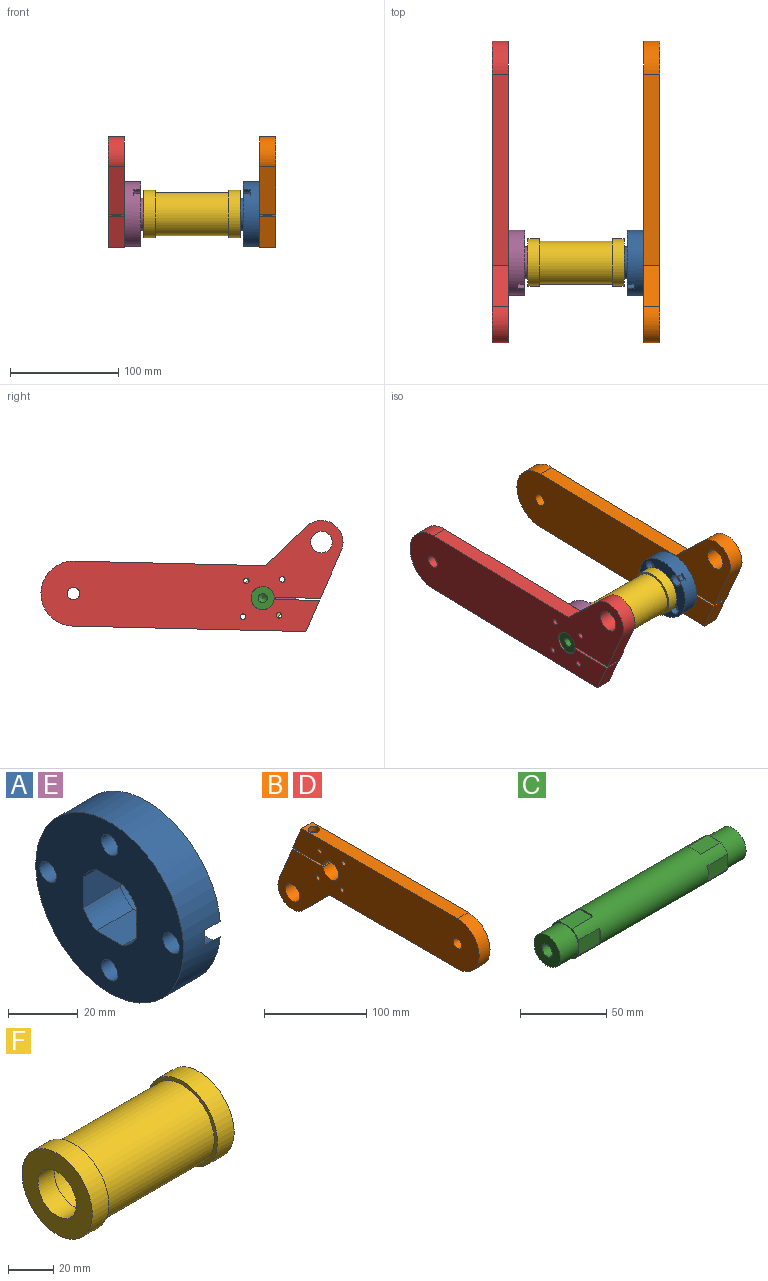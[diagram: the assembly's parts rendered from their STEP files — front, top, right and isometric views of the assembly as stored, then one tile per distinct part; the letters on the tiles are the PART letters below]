
ASSEMBLY  parts=6 mates=4
PART A: 27 faces, bbox 18x60x60 mm
  f0: cylinder r=12mm len=15mm, axis (-1,0,0), area 117mm2, adj f6,f7,f24,f26
  f1: cylinder r=12mm len=15mm, axis (-1,0,0), area 117mm2, adj f6,f7,f23,f25
  f2: cylinder r=12mm len=15mm, axis (-1,0,0), area 117mm2, adj f6,f7,f24,f25
  f3: cylinder r=12mm len=15mm, axis (-1,0,0), area 117mm2, adj f6,f7,f23,f26
  f4: cylinder r=30mm len=60mm, axis (-1,0,0), area 2760mm2, adj f5,f7,f14,f15,f20,f21
  f5: plane 60x59.77mm, normal (1,0,0), area 1758.7mm2, adj f4,f9,f13,f15,f19,f21
  f6: plane 25.75x25.75mm, normal (1,0,0), area 104.3mm2, adj f0,f1,f2,f3,f8,f23,f24,f25
  f7: plane 60x60mm, normal (-1,0,0), area 2267.6mm2, adj f0,f1,f2,f3,f4,f11,f16,f17
  f8: cylinder r=12.88mm len=25.75mm, axis (-1,0,0), area 242.7mm2, adj f6,f10
  f9: cylinder r=14.76mm len=29.53mm, axis (-1,0,0), area 278.3mm2, adj f5,f10
  f10: plane 29.53x29.53mm, normal (1,0,0), area 164mm2, adj f8,f9
  f11: cylinder r=3.38mm len=8.65mm, axis (1,0,0), area 183.6mm2, adj f7,f12
  f12: plane 11.11x11.11mm, normal (1,0,0), area 61.1mm2, adj f11,f13
  f13: cylinder r=5.56mm len=11.11mm, axis (1,0,0), area 221.7mm2, adj f5,f12
  f14: plane 11.11x10.56mm, normal (1,0,0), area 59.1mm2, adj f4,f15,f16
  f15: cylinder r=5.56mm len=11.11mm, axis (1,0,0), area 186.6mm2, adj f4,f5,f14
  f16: cylinder r=3.38mm len=8.65mm, axis (1,0,0), area 183.6mm2, adj f7,f14
  f17: cylinder r=3.38mm len=8.65mm, axis (1,0,0), area 183.6mm2, adj f7,f18
  f18: plane 11.11x11.11mm, normal (1,0,0), area 61.1mm2, adj f17,f19
  f19: cylinder r=5.56mm len=11.11mm, axis (1,0,0), area 221.7mm2, adj f5,f18
  f20: plane 11.11x10.56mm, normal (1,0,0), area 59.1mm2, adj f4,f21,f22
  f21: cylinder r=5.56mm len=11.11mm, axis (1,0,0), area 186.6mm2, adj f4,f5,f20
  f22: cylinder r=3.38mm len=8.65mm, axis (1,0,0), area 183.6mm2, adj f7,f20
  f23: plane 15x10.67mm, normal (0,0,-1), area 160mm2, adj f1,f3,f6,f7
  f24: plane 15x10.67mm, normal (0,0,1), area 160mm2, adj f0,f2,f6,f7
  f25: plane 15x10.67mm, normal (0,-1,0), area 160mm2, adj f1,f2,f6,f7
  f26: plane 15x10.67mm, normal (0,1,0), area 160mm2, adj f0,f3,f6,f7
PART B: 23 faces, bbox 15x278x103 mm
  f0: plane 278.03x103.03mm, normal (1,0,0), area 16118.8mm2, adj f1,f2,f3,f4,f6,f7,f8,f9
  f1: plane 29x15mm, normal (0,0.93,0.38), area 469.8mm2, adj f0,f3,f5,f15
  f2: plane 176.72x15mm, normal (0,0,-1), area 2650.7mm2, adj f0,f4,f5,f11
  f3: plane 215.75x15mm, normal (0,0,1), area 3139.3mm2, adj f0,f1,f4,f5,f19
  f4: cylinder r=30mm len=60mm, axis (-1,0,0), area 1413.7mm2, adj f0,f2,f3,f5
  f5: plane 278.03x103.03mm, normal (-1,0,0), area 16118.8mm2, adj f1,f2,f3,f4,f6,f7,f8,f9
  f6: cylinder r=5.75mm len=15mm, axis (1,0,0), area 542.3mm2, adj f0,f5
  f7: cylinder r=2.55mm len=15mm, axis (1,0,0), area 240.6mm2, adj f0,f5
  f8: cylinder r=2.55mm len=15mm, axis (1,0,0), area 240.6mm2, adj f0,f5
  f9: cylinder r=2.55mm len=15mm, axis (1,0,0), area 240.6mm2, adj f0,f5
  f10: cylinder r=2.55mm len=15mm, axis (1,0,0), area 240.6mm2, adj f0,f5
  f11: plane 37.18x37.18mm, normal (0,-0.71,-0.71), area 788.6mm2, adj f0,f2,f5,f12
  f12: cylinder r=20mm len=34.14mm, axis (1,0,0), area 823.1mm2, adj f0,f5,f11,f14
  f13: cylinder r=10mm len=20mm, axis (1,0,0), area 942.5mm2, adj f0,f5
  f14: plane 44.48x18.15mm, normal (0,0.93,0.38), area 720.6mm2, adj f0,f5,f12,f16
  f15: plane 41.88x15mm, normal (0,0,-1), area 592.4mm2, adj f0,f1,f5,f17,f22
  f16: plane 42.7x15mm, normal (0,0,1), area 617.5mm2, adj f0,f5,f14,f20,f22
  f17: cylinder r=3.38mm len=22.65mm, axis (0,0,1), area 480.8mm2, adj f15,f18
  f18: plane 11.11x11.11mm, normal (0,0,1), area 61.1mm2, adj f17,f19
  f19: cylinder r=5.56mm len=11.11mm, axis (0,0,1), area 221.7mm2, adj f3,f18
  f20: cylinder r=2.71mm len=29mm, axis (0,0,1), area 492.9mm2, adj f16,f21
  f21: cone r=0mm half-angle=59deg, axis (0,0,1), area 26.8mm2, adj f20
  f22: cylinder r=10.75mm len=21.5mm, axis (1,0,0), area 983.1mm2, adj f0,f5,f15,f16
PART C: 33 faces, bbox 152x24x24 mm
  f0: plane 17x10.67mm, normal (0,-1,0), area 181.3mm2, adj f12,f24,f26,f28
  f1: plane 17x10.67mm, normal (0,0,1), area 181.3mm2, adj f13,f24,f26,f27
  f2: plane 17x10.67mm, normal (0,1,0), area 181.3mm2, adj f14,f24,f27,f29
  f3: plane 17x10.67mm, normal (0,0,-1), area 181.3mm2, adj f15,f24,f28,f29
  f4: plane 21.5x21.5mm, normal (1,0,0), area 307.2mm2, adj f5,f7
  f5: cylinder r=4.22mm len=20mm, axis (1,0,0), area 529.8mm2, adj f4,f6
  f6: cone r=0mm half-angle=59deg, axis (1,0,0), area 65.2mm2, adj f5
  f7: cylinder r=10.75mm len=21.5mm, axis (1,0,0), area 1013.2mm2, adj f4,f8,f9,f10,f11
  f8: plane 10.75x10.75mm, normal (1,0,0), area 13.4mm2, adj f7,f20,f23,f24
  f9: plane 10.75x10.75mm, normal (1,0,0), area 13.4mm2, adj f7,f20,f21,f24
  f10: plane 10.75x10.75mm, normal (1,0,0), area 13.4mm2, adj f7,f21,f22,f24
  f11: plane 10.75x10.75mm, normal (1,0,0), area 13.4mm2, adj f7,f22,f23,f24
  f12: plane 10.67x1.25mm, normal (-1,0,0), area 9mm2, adj f0,f24
  f13: plane 10.67x1.25mm, normal (-1,0,0), area 9mm2, adj f1,f24
  f14: plane 10.67x1.25mm, normal (-1,0,0), area 9mm2, adj f2,f24
  f15: plane 10.67x1.25mm, normal (-1,0,0), area 9mm2, adj f3,f24
  f16: plane 10.67x1.25mm, normal (1,0,0), area 9mm2, adj f23,f24
  f17: plane 10.67x1.25mm, normal (1,0,0), area 9mm2, adj f21,f24
  f18: plane 10.67x1.25mm, normal (1,0,0), area 9mm2, adj f20,f24
  f19: plane 10.67x1.25mm, normal (1,0,0), area 9mm2, adj f22,f24
  f20: plane 17x10.67mm, normal (0,0,1), area 181.3mm2, adj f8,f9,f18,f24
  f21: plane 17x10.67mm, normal (0,-1,0), area 181.3mm2, adj f9,f10,f17,f24
  f22: plane 17x10.67mm, normal (0,0,-1), area 181.3mm2, adj f10,f11,f19,f24
  f23: plane 17x10.67mm, normal (0,1,0), area 181.3mm2, adj f8,f11,f16,f24
  f24: cylinder r=12mm len=122mm, axis (-1,0,0), area 7695.5mm2, adj f0,f1,f2,f3,f8,f9,f10,f11
  f25: cylinder r=10.75mm len=21.5mm, axis (-1,0,0), area 1013.2mm2, adj f26,f27,f28,f29,f32
  f26: plane 10.75x10.75mm, normal (-1,0,0), area 13.4mm2, adj f0,f1,f24,f25
  f27: plane 10.75x10.75mm, normal (-1,0,0), area 13.4mm2, adj f1,f2,f24,f25
  f28: plane 10.75x10.75mm, normal (-1,0,0), area 13.4mm2, adj f0,f3,f24,f25
  f29: plane 10.75x10.75mm, normal (-1,0,0), area 13.4mm2, adj f2,f3,f24,f25
  f30: cone r=0mm half-angle=59deg, axis (-1,0,0), area 65.2mm2, adj f31
  f31: cylinder r=4.22mm len=20mm, axis (-1,0,0), area 529.8mm2, adj f30,f32
  f32: plane 21.5x21.5mm, normal (-1,0,0), area 307.2mm2, adj f25,f31
PART D: same geometry as B
PART E: same geometry as A
PART F: 12 faces, bbox 88.8x44x44 mm
  f0: cylinder r=15mm len=68mm, axis (-1,0,0), area 6408.8mm2, adj f2,f7
  f1: cylinder r=20mm len=68mm, axis (-1,0,0), area 8545.1mm2, adj f6,f11
  f2: plane 30x30mm, normal (-1,0,0), area 254.5mm2, adj f0,f4
  f3: cylinder r=22mm len=44mm, axis (-1,0,0), area 1439.5mm2, adj f5,f6
  f4: cylinder r=12mm len=24mm, axis (-1,0,0), area 785.2mm2, adj f2,f5
  f5: plane 44x44mm, normal (1,0,0), area 1068.1mm2, adj f3,f4
  f6: plane 44x44mm, normal (-1,0,0), area 263.9mm2, adj f1,f3
  f7: plane 30x30mm, normal (1,0,0), area 254.5mm2, adj f0,f9
  f8: cylinder r=22mm len=44mm, axis (1,0,0), area 1439.5mm2, adj f10,f11
  f9: cylinder r=12mm len=24mm, axis (1,0,0), area 785.2mm2, adj f7,f10
  f10: plane 44x44mm, normal (-1,0,0), area 1068.1mm2, adj f8,f9
  f11: plane 44x44mm, normal (1,0,0), area 263.9mm2, adj f1,f8
PLACE A rot(axis=(0,0.37,0.93),180deg) t=(26.37,-27.61,13.72)mm
PLACE B rot(axis=(-1,0,0),178.6deg) t=(26.37,-27.61,13.72)mm
PLACE C rot(axis=(1,0,0),1.4deg) t=(-36.04,-27.61,13.72)mm
PLACE D rot(axis=(-1,0,0),178.6deg) t=(-113.46,-27.61,13.72)mm
PLACE E rot(axis=(-1,0,0),43.6deg) t=(-98.46,-27.61,13.72)mm
PLACE F t=(-36.04,-27.61,13.72)mm fixed
MATE planar E.f0 <-> F.f0  axis (1,0,0) through (-80.46,-27.61,13.72)mm
MATE cylindrical C.f5 <-> F.f0  axis (-1,0,0) through (-36.04,-27.61,13.72)mm
MATE planar A.f0 <-> F.f0  axis (-1,0,0) through (8.37,-27.61,13.72)mm
MATE planar D.f9 <-> E.f0  axis (1,0,0) through (-98.46,-45.7,30.98)mm
